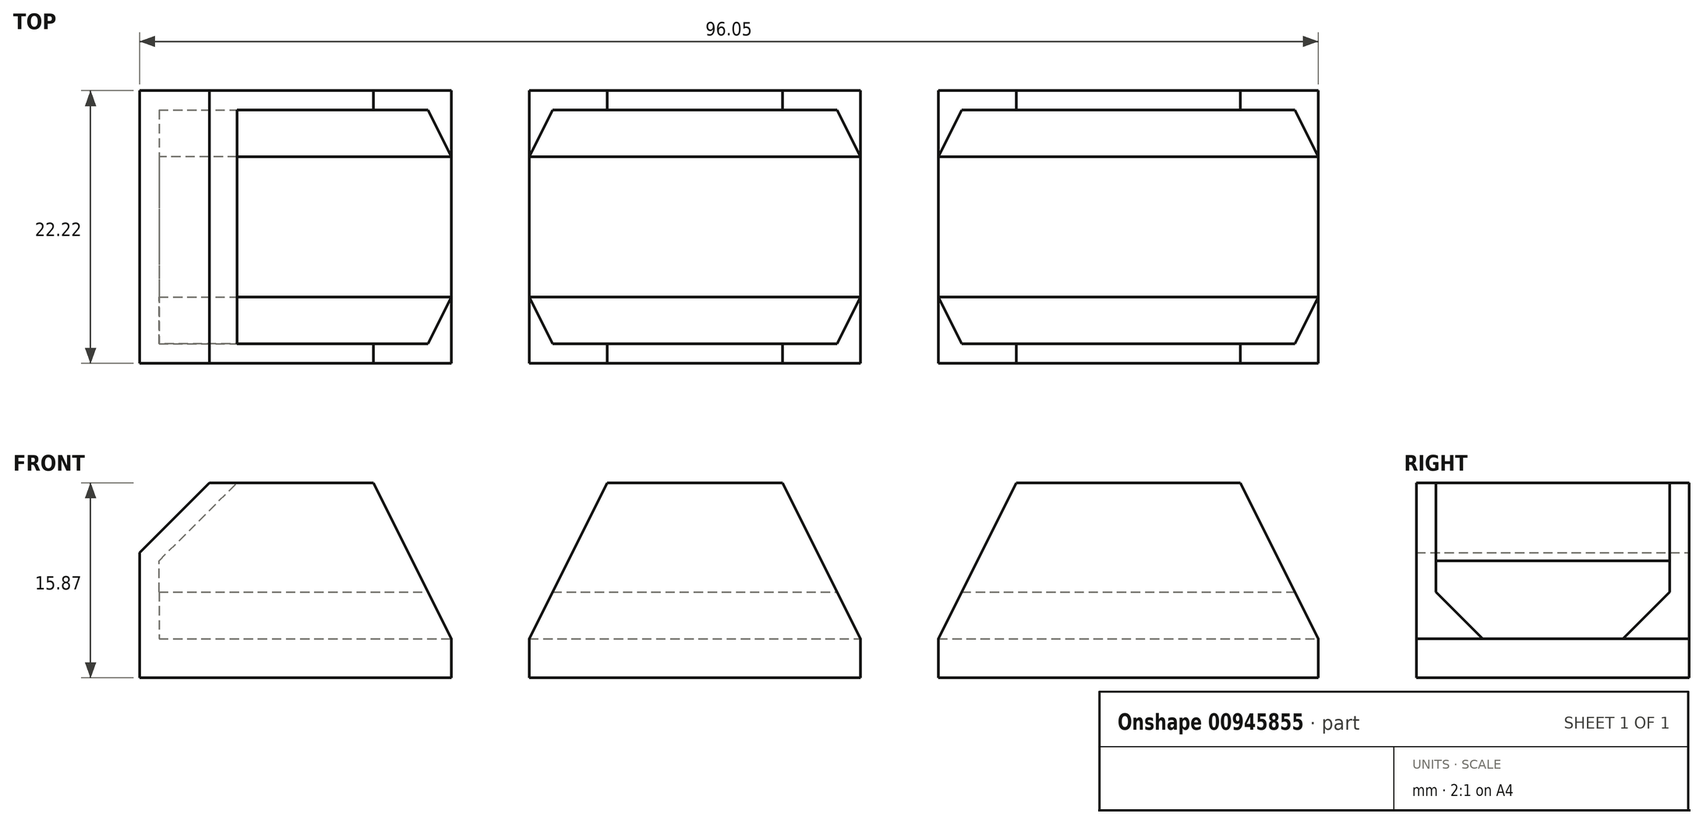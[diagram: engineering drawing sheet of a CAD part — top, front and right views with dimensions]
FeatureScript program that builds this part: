
annotation { "Feature Type Name" : "Feature", "Feature Type Description" : "" }
export const myFeature = defineFeature(function(context is Context, id is Id, definition is map)
    precondition{}
    {
        {
            var Q0;
            Q0=qCreatedBy(makeId("Front.planeOp"),FACE);
            var sketch = newSketch(context, id + "F0", { "sketchPlane" : qUnion([Q0])});
            skLineSegment(sketch, "E0.bottom", {"start": v(10.32, 0) * mm, "end": v(-16.67, 0) * mm});
            skLineSegment(sketch, "E0.top", {"start": v(10.32, -3.18) * mm, "end": v(-16.67, -3.18) * mm});
            skLineSegment(sketch, "E0.left", {"start": v(10.32, 0) * mm, "end": v(10.32, -3.17) * mm});
            skLineSegment(sketch, "E0.right", {"start": v(-16.67, 0) * mm, "end": v(-16.67, -3.18) * mm});
            skLineSegment(sketch, "E1", {"start": v(-16.67, 0) * mm, "end": v(-10.32, 0) * mm});
            skLineSegment(sketch, "E2", {"start": v(-10.32, 0) * mm, "end": v(-10.32, 12.7) * mm});
            skLineSegment(sketch, "E3", {"start": v(10.32, 0) * mm, "end": v(3.97, 0) * mm});
            skLineSegment(sketch, "E4", {"start": v(3.97, 0) * mm, "end": v(3.97, 12.7) * mm});
            skLineSegment(sketch, "E5", {"start": v(3.97, 12.7) * mm, "end": v(-10.32, 12.7) * mm});
            skLineSegment(sketch, "E6", {"start": v(-10.32, 12.7) * mm, "end": v(-16.67, 0) * mm});
            skLineSegment(sketch, "E7", {"start": v(3.97, 12.7) * mm, "end": v(10.32, 0) * mm});
            skLineSegment(sketch, "E8", {"start": v(-16.67, 0) * mm, "end": v(-23.02, 0) * mm});
            skLineSegment(sketch, "E9", {"start": v(-23.02, 0) * mm, "end": v(-23.02, -3.18) * mm});
            skLineSegment(sketch, "E10", {"start": v(10.32, -3.17) * mm, "end": v(16.67, -3.17) * mm});
            skLineSegment(sketch, "E11", {"start": v(16.67, -3.17) * mm, "end": v(47.63, -3.17) * mm});
            skLineSegment(sketch, "E12", {"start": v(47.63, -3.17) * mm, "end": v(47.63, 0) * mm});
            skLineSegment(sketch, "E13", {"start": v(47.63, 0) * mm, "end": v(16.67, 0) * mm});
            skLineSegment(sketch, "E14", {"start": v(16.67, 0) * mm, "end": v(16.67, -3.17) * mm});
            skLineSegment(sketch, "E15", {"start": v(-23.02, 0) * mm, "end": v(-46.83, 0) * mm});
            skLineSegment(sketch, "E16", {"start": v(-46.83, 0) * mm, "end": v(-46.83, -3.17) * mm});
            skLineSegment(sketch, "E17", {"start": v(-46.83, -3.18) * mm, "end": v(-23.02, -3.18) * mm});
            skLineSegment(sketch, "E18", {"start": v(-23.02, 0) * mm, "end": v(-29.37, 0) * mm});
            skLineSegment(sketch, "E19", {"start": v(-29.37, 0) * mm, "end": v(-29.37, 12.7) * mm});
            skLineSegment(sketch, "E20", {"start": v(-46.83, 0) * mm, "end": v(-40.48, 0) * mm});
            skLineSegment(sketch, "E21", {"start": v(-40.48, 0) * mm, "end": v(-40.48, 12.7) * mm});
            skLineSegment(sketch, "E22", {"start": v(-29.37, 12.7) * mm, "end": v(-23.02, 0) * mm});
            skLineSegment(sketch, "E23", {"start": v(-46.83, 0) * mm, "end": v(-46.83, 6.35) * mm});
            skLineSegment(sketch, "E24", {"start": v(-46.83, 6.35) * mm, "end": v(-40.48, 12.7) * mm});
            skLineSegment(sketch, "E25", {"start": v(16.67, 0) * mm, "end": v(23.02, 0) * mm});
            skLineSegment(sketch, "E26", {"start": v(23.02, 0) * mm, "end": v(23.02, 12.7) * mm});
            skLineSegment(sketch, "E27", {"start": v(47.63, 0) * mm, "end": v(41.28, 0) * mm});
            skLineSegment(sketch, "E28", {"start": v(41.28, 0) * mm, "end": v(41.28, 12.7) * mm});
            skLineSegment(sketch, "E29", {"start": v(41.28, 12.7) * mm, "end": v(23.02, 12.7) * mm});
            skLineSegment(sketch, "E30", {"start": v(23.02, 12.7) * mm, "end": v(16.67, 0) * mm});
            skLineSegment(sketch, "E31", {"start": v(41.28, 12.7) * mm, "end": v(47.63, 0) * mm});
            skLineSegment(sketch, "E32", {"start": v(-46.83, -3.17) * mm, "end": v(-48.42, -3.17) * mm});
            skLineSegment(sketch, "E33", {"start": v(-48.42, -3.17) * mm, "end": v(-48.42, 6.35) * mm});
            skLineSegment(sketch, "E34", {"start": v(-48.42, 7) * mm, "end": v(-48.42, 6.35) * mm});
            skLineSegment(sketch, "E35", {"start": v(-40.48, 12.7) * mm, "end": v(-42.73, 12.7) * mm});
            skLineSegment(sketch, "E36", {"start": v(-42.73, 12.7) * mm, "end": v(-48.42, 7) * mm});
            skLineSegment(sketch, "E37", {"start": v(-40.48, 12.7) * mm, "end": v(-29.37, 12.7) * mm});
            skSolve(sketch);
        }
        {
            var Q0;
            {var subQ2=sQuery(id+"F0.wireOp",EDGE,"E21");Q0=makeQuery(id+"F0.imprint","IMPRINT",FACE,{"disambiguationData":[TD([[makeQuery(id+"F0.imprint","IMPRINT",EDGE,{"derivedFrom":subQ2}),1.0]])]});}
            var Q1;
            {var subQ2=sQuery(id+"F0.wireOp",EDGE,"E2");Q1=makeQuery(id+"F0.imprint","IMPRINT",FACE,{"disambiguationData":[TD([[makeQuery(id+"F0.imprint","IMPRINT",EDGE,{"derivedFrom":subQ2}),1.0]])]});}
            var Q2;
            {var subQ0=sQuery(id+"F0.wireOp",EDGE,"E4");Q2=makeQuery(id+"F0.imprint","IMPRINT",FACE,{"disambiguationData":[TD([[makeQuery(id+"F0.imprint","IMPRINT",EDGE,{"derivedFrom":subQ0}),-1.0]])]});}
            var Q3;
            {var subQ2=sQuery(id+"F0.wireOp",EDGE,"E19");Q3=makeQuery(id+"F0.imprint","IMPRINT",FACE,{"disambiguationData":[TD([[makeQuery(id+"F0.imprint","IMPRINT",EDGE,{"derivedFrom":subQ2}),-1.0]])]});}
            var Q4;
            {var subQ2=sQuery(id+"F0.wireOp",EDGE,"E26");Q4=makeQuery(id+"F0.imprint","IMPRINT",FACE,{"disambiguationData":[TD([[makeQuery(id+"F0.imprint","IMPRINT",EDGE,{"derivedFrom":subQ2}),1.0]])]});}
            var Q5;
            {var subQ2=sQuery(id+"F0.wireOp",EDGE,"E28");Q5=makeQuery(id+"F0.imprint","IMPRINT",FACE,{"disambiguationData":[TD([[makeQuery(id+"F0.imprint","IMPRINT",EDGE,{"derivedFrom":subQ2}),-1.0]])]});}
            var Q6;
            Q6=makeQuery(id+"F0.imprint","IMPRINT",FACE,{"disambiguationData":[TD([[makeQuery(id+"F0.imprint","IMPRINT",EDGE,{"derivedFrom":sQuery(id+"F0.wireOp",EDGE,"E0.top")}),-1.0]])]});
            var Q7;
            {var subQ2=sQuery(id+"F0.wireOp",EDGE,"E2");Q7=makeQuery(id+"F0.imprint","IMPRINT",FACE,{"disambiguationData":[TD([[makeQuery(id+"F0.imprint","IMPRINT",EDGE,{"derivedFrom":subQ2}),-1.0]])]});}
            var Q8;
            Q8=makeQuery(id+"F0.imprint","IMPRINT",FACE,{"disambiguationData":[TD([[makeQuery(id+"F0.imprint","IMPRINT",EDGE,{"derivedFrom":sQuery(id+"F0.wireOp",EDGE,"E11")}),1.0]])]});
            var Q9;
            {var subQ2=sQuery(id+"F0.wireOp",EDGE,"E26");Q9=makeQuery(id+"F0.imprint","IMPRINT",FACE,{"disambiguationData":[TD([[makeQuery(id+"F0.imprint","IMPRINT",EDGE,{"derivedFrom":subQ2}),-1.0]])]});}
            var Q10;
            Q10=makeQuery(id+"F0.imprint","IMPRINT",FACE,{"disambiguationData":[TD([[makeQuery(id+"F0.imprint","IMPRINT",EDGE,{"derivedFrom":sQuery(id+"F0.wireOp",EDGE,"E16")}),-1.0]])]});
            var Q11;
            Q11=makeQuery(id+"F0.imprint","IMPRINT",FACE,{"disambiguationData":[TD([[makeQuery(id+"F0.imprint","IMPRINT",EDGE,{"derivedFrom":sQuery(id+"F0.wireOp",EDGE,"LXoh7koV-5Cl1-UZ9v-uWf4-F4D3IbVnI419")}),1.0]])]});
            var Q12;
            {var subQ1=sQuery(id+"F0.wireOp",EDGE,"E9");Q12=makeQuery(id+"F0.imprint","IMPRINT",FACE,{"disambiguationData":[TD([[makeQuery(id+"F0.imprint","IMPRINT",EDGE,{"derivedFrom":subQ1}),-1.0]])]});}
            var Q13;
            {var subQ0=sQuery(id+"F0.wireOp",EDGE,"E19");Q13=makeQuery(id+"F0.imprint","IMPRINT",FACE,{"disambiguationData":[TD([[makeQuery(id+"F0.imprint","IMPRINT",EDGE,{"derivedFrom":subQ0}),1.0]])]});}
            extrude(context, id + "F1", {"entities" : qUnion([Q0, Q1, Q2, Q3, Q4, Q5, Q6, Q7, Q8, Q9, Q10, Q11, Q12, Q13]), "endBound" : BoundingType.SYMMETRIC, "depth" : 22.22 * mm, "offsetDistance" : 25.4 * mm});
        }
        {
            var Q0;
            {var subQ2=sQuery(id+"F0.wireOp",EDGE,"E21");Q0=makeQuery(id+"F0.imprint","IMPRINT",FACE,{"disambiguationData":[TD([[makeQuery(id+"F0.imprint","IMPRINT",EDGE,{"derivedFrom":subQ2}),1.0]])]});}
            var Q1;
            {var subQ0=sQuery(id+"F0.wireOp",EDGE,"E19");Q1=makeQuery(id+"F0.imprint","IMPRINT",FACE,{"disambiguationData":[TD([[makeQuery(id+"F0.imprint","IMPRINT",EDGE,{"derivedFrom":subQ0}),1.0]])]});}
            var Q2;
            {var subQ2=sQuery(id+"F0.wireOp",EDGE,"E19");Q2=makeQuery(id+"F0.imprint","IMPRINT",FACE,{"disambiguationData":[TD([[makeQuery(id+"F0.imprint","IMPRINT",EDGE,{"derivedFrom":subQ2}),-1.0]])]});}
            var Q3;
            {var subQ2=sQuery(id+"F0.wireOp",EDGE,"E2");Q3=makeQuery(id+"F0.imprint","IMPRINT",FACE,{"disambiguationData":[TD([[makeQuery(id+"F0.imprint","IMPRINT",EDGE,{"derivedFrom":subQ2}),-1.0]])]});}
            var Q4;
            {var subQ2=sQuery(id+"F0.wireOp",EDGE,"E2");Q4=makeQuery(id+"F0.imprint","IMPRINT",FACE,{"disambiguationData":[TD([[makeQuery(id+"F0.imprint","IMPRINT",EDGE,{"derivedFrom":subQ2}),1.0]])]});}
            var Q5;
            {var subQ0=sQuery(id+"F0.wireOp",EDGE,"E4");Q5=makeQuery(id+"F0.imprint","IMPRINT",FACE,{"disambiguationData":[TD([[makeQuery(id+"F0.imprint","IMPRINT",EDGE,{"derivedFrom":subQ0}),-1.0]])]});}
            var Q6;
            {var subQ2=sQuery(id+"F0.wireOp",EDGE,"E26");Q6=makeQuery(id+"F0.imprint","IMPRINT",FACE,{"disambiguationData":[TD([[makeQuery(id+"F0.imprint","IMPRINT",EDGE,{"derivedFrom":subQ2}),1.0]])]});}
            var Q7;
            {var subQ2=sQuery(id+"F0.wireOp",EDGE,"E26");Q7=makeQuery(id+"F0.imprint","IMPRINT",FACE,{"disambiguationData":[TD([[makeQuery(id+"F0.imprint","IMPRINT",EDGE,{"derivedFrom":subQ2}),-1.0]])]});}
            var Q8;
            {var subQ2=sQuery(id+"F0.wireOp",EDGE,"E28");Q8=makeQuery(id+"F0.imprint","IMPRINT",FACE,{"disambiguationData":[TD([[makeQuery(id+"F0.imprint","IMPRINT",EDGE,{"derivedFrom":subQ2}),-1.0]])]});}
            extrude(context, id + "F2", {"entities" : qUnion([Q0, Q1, Q2, Q3, Q4, Q5, Q6, Q7, Q8]), "operationType" : NewBodyOperationType.REMOVE, "endBound" : BoundingType.SYMMETRIC, "oppositeDirection" : true, "depth" : 19.05 * mm, "offsetDistance" : 25.4 * mm});
        }
        {
            var Q0;
            Q0=makeQuery(id+"F2.boolean.opBoolean","COPY",EDGE,{"derivedFrom":makeQuery(id+"F2.opExtrude","CAP_EDGE",EDGE,{"disambiguationData":[OSD([sQuery(id+"F0.wireOp",EDGE,"E15")])],"isStart":true})});
            var Q1;
            Q1=makeQuery(id+"F2.boolean.opBoolean","COPY",EDGE,{"derivedFrom":makeQuery(id+"F2.opExtrude","CAP_EDGE",EDGE,{"disambiguationData":[OSD([sQuery(id+"F0.wireOp",EDGE,"E15")])],"isStart":false})});
            var Q2;
            Q2=makeQuery(id+"F2.boolean.opBoolean","COPY",EDGE,{"derivedFrom":makeQuery(id+"F2.opExtrude","CAP_EDGE",EDGE,{"disambiguationData":[OSD([sQuery(id+"F0.wireOp",EDGE,"E0.bottom")])],"isStart":false})});
            var Q3;
            Q3=makeQuery(id+"F2.boolean.opBoolean","COPY",EDGE,{"derivedFrom":makeQuery(id+"F2.opExtrude","CAP_EDGE",EDGE,{"disambiguationData":[OSD([sQuery(id+"F0.wireOp",EDGE,"E13")])],"isStart":false})});
            var Q4;
            Q4=makeQuery(id+"F2.boolean.opBoolean","COPY",EDGE,{"derivedFrom":makeQuery(id+"F2.opExtrude","CAP_EDGE",EDGE,{"disambiguationData":[OSD([sQuery(id+"F0.wireOp",EDGE,"E0.bottom")])],"isStart":true})});
            var Q5;
            Q5=makeQuery(id+"F2.boolean.opBoolean","COPY",EDGE,{"derivedFrom":makeQuery(id+"F2.opExtrude","CAP_EDGE",EDGE,{"disambiguationData":[OSD([sQuery(id+"F0.wireOp",EDGE,"E13")])],"isStart":true})});
            chamfer(context, id + "F3", {"entities" : qUnion([Q0, Q1, Q2, Q3, Q4, Q5]), "width" : 3.8 * mm, "tangentPropagation" : true});
        }
    });
